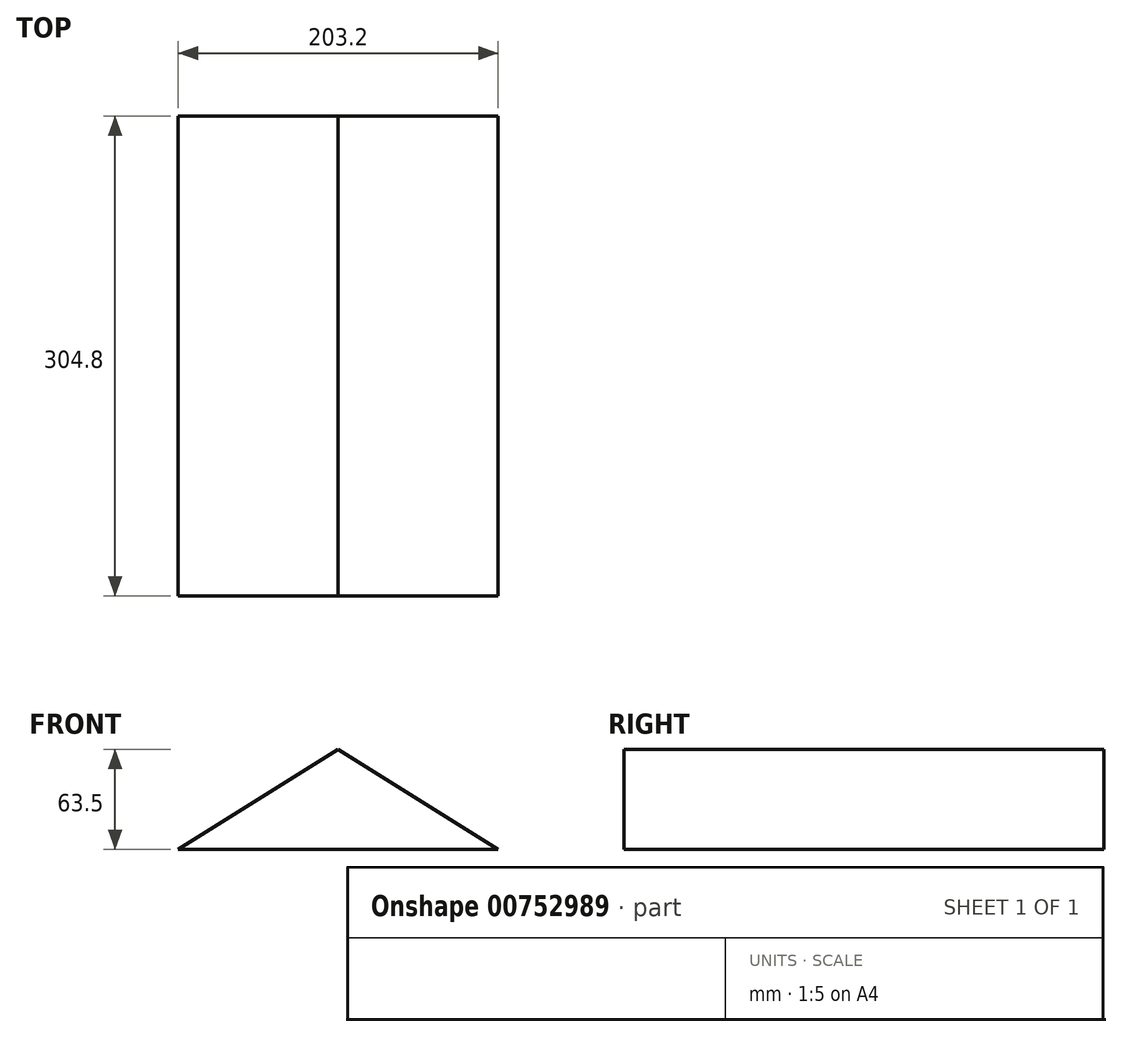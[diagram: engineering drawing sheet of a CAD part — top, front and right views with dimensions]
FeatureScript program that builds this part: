
annotation { "Feature Type Name" : "Feature", "Feature Type Description" : "" }
export const myFeature = defineFeature(function(context is Context, id is Id, definition is map)
    precondition{}
    {
        {
            var Q0;
            Q0=qCreatedBy(makeId("Front.planeOp"),FACE);
            var sketch = newSketch(context, id + "F0", { "sketchPlane" : qUnion([Q0])});
            skLineSegment(sketch, "E0", {"start": v(-120.45, -2.73) * mm, "end": v(82.75, -2.73) * mm});
            skLineSegment(sketch, "E1", {"start": v(-18.85, -2.73) * mm, "end": v(-18.85, 60.77) * mm});
            skLineSegment(sketch, "E2", {"start": v(-18.85, 60.77) * mm, "end": v(82.75, -2.73) * mm});
            skLineSegment(sketch, "E3", {"start": v(-18.85, 60.77) * mm, "end": v(-120.45, -2.73) * mm});
            skSolve(sketch);
        }
        {
            var Q0;
            Q0 = qSketchRegion(id + "F0", true);
            extrude(context, id + "F1", {"entities" : qUnion([Q0]), "depth" : 304.8 * mm, "offsetDistance" : 25.4 * mm});
        }
    });
